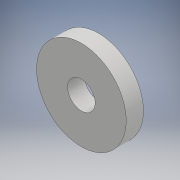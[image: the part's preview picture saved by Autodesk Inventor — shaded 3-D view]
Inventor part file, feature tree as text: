
AUTODESK INVENTOR PART (.ipt)
format: ipt  version: 2018 (Build 220112000, 112)  size: 98,816 bytes
history: native  units: mm
features: other x1, extrude x1, sketch x1
ambient origin geometry x8: Origin, YZ Plane, XZ Plane, XY Plane, X Axis, Y Axis, Z Axis, Center Point
bodies: Body1 (feature_tree)
feature tree (3):
  other  "Sólido1"
  extrude  "Extrusión1"  Depth=5.0mm
  sketch  "Boceto1"  dims[d0=8.0mm d1=26.0mm d2=5.0mm d3=0.0mm]
